# Revit family: FL6020001_PT ROLLO_FLAT
name_source: partatom
category: Furniture
revit_build: Autodesk Revit 2016 (Build: 20150714_1515(x64)
units: mm (PartAtom-declared; Revit-internal decimal feet)

## family parameters
Always vertical = Yes
Cut with Voids When Loaded = No
OmniClass Number = 23.40.20.14.17
OmniClass Title = Residential Tables and Cabinets
Room Calculation Point = No
Shared = Yes
Work Plane-Based = No

## types (3) — shared parameters
Base Material = Wood - Birch
Top Material = Laminate - Ivory, Matte

## per-type parameters (varying)
| type | Height | Length | Width |
| 0610 x 0160mm | 762 mm  [stored 2.5 ft] | 610 mm | 610 mm |
| 0762 x 0762mm | 457 mm  [stored 1.49934 ft] | 762 mm  [stored 2.5 ft] | 762 mm  [stored 2.5 ft] |
| 0610 x 0915mm | 762 mm  [stored 2.5 ft] | 610 mm | 915 mm |

note: [stored X ft] marks values corroborated as IEEE doubles in the binary element streams (Revit-internal decimal feet)

## geometry (parser evidence)
native form markers: Sweep x1
no freeform markers — native parametric forms only
